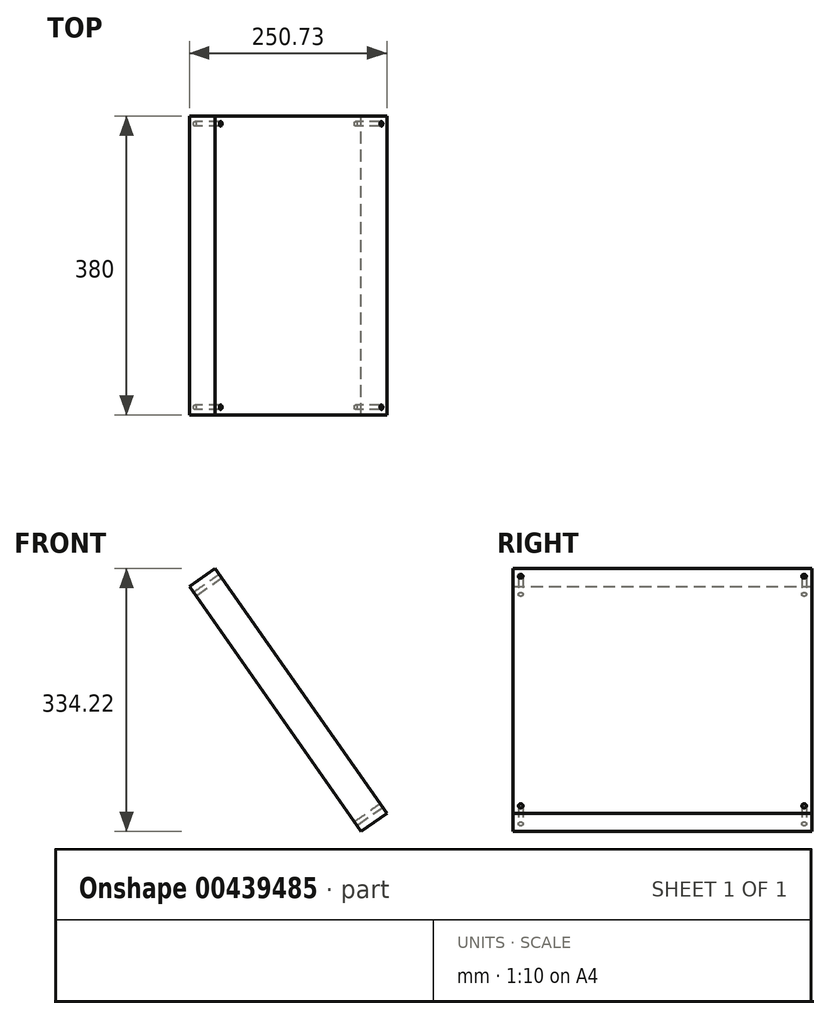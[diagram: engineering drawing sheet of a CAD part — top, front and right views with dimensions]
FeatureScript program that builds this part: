
annotation { "Feature Type Name" : "Feature", "Feature Type Description" : "" }
export const myFeature = defineFeature(function(context is Context, id is Id, definition is map)
    precondition{}
    {
        {
            var Q0;
            Q0=qCreatedBy(makeId("Front.planeOp"),FACE);
            var sketch = newSketch(context, id + "F0", { "sketchPlane" : qUnion([Q0])});
            skLineSegment(sketch, "E0.bottom", {"start": v(-138.5, 149.95) * mm, "end": v(79.46, -161.32) * mm});
            skLineSegment(sketch, "E0.top", {"start": v(-171.27, 127.01) * mm, "end": v(46.69, -184.27) * mm});
            skLineSegment(sketch, "E0.left", {"start": v(-138.5, 149.95) * mm, "end": v(-171.27, 127.01) * mm});
            skLineSegment(sketch, "E0.right", {"start": v(79.46, -161.32) * mm, "end": v(46.69, -184.27) * mm});
            skSolve(sketch);
        }
        {
            var Q0;
            Q0=makeQuery(id+"F0.imprint","IMPRINT",FACE,{"disambiguationData":[TD([[makeQuery(id+"F0.imprint","IMPRINT",EDGE,{"derivedFrom":sQuery(id+"F0.wireOp",EDGE,"E0.bottom")}),-1.0]])]});
            extrude(context, id + "F1", {"entities" : qUnion([Q0]), "depth" : 380 * mm});
        }
        {
            var Q0;
            Q0=makeQuery(id+"F1.opExtrude","SWEPT_FACE",FACE,{"disambiguationData":[OSD([sQuery(id+"F0.wireOp",EDGE,"E0.top")])]});
            var sketch = newSketch(context, id + "F2", { "sketchPlane" : qUnion([Q0])});
            skCircle(sketch, "E1", {"center": v(370, 190.28) * mm, "radius": 3 * mm});
            skLineSegment(sketch, "E2.0", {"start": v(380, 202.28) * mm, "end": v(0, 202.28) * mm});
            skLineSegment(sketch, "E3.0.0", {"start": v(0, 202.28) * mm, "end": v(0, -177.72) * mm});
            skLineSegment(sketch, "E3.0.1", {"start": v(0, -177.72) * mm, "end": v(380, -177.72) * mm});
            skLineSegment(sketch, "E4", {"start": v(190, 202.28) * mm, "end": v(190, -177.72) * mm, "construction": true});
            skLineSegment(sketch, "E5", {"start": v(380, 12.28) * mm, "end": v(190, 12.28) * mm, "construction": true});
            skCircle(sketch, "E6.MirrorC", {"center": v(370, -165.72) * mm, "radius": 3 * mm});
            skCircle(sketch, "E7.MirrorC", {"center": v(10, -165.72) * mm, "radius": 3 * mm});
            skCircle(sketch, "E8.MirrorC", {"center": v(10, 190.28) * mm, "radius": 3 * mm});
            skSolve(sketch);
        }
        {
            var Q0;
            Q0 = qSketchRegion(id + "F2", true);
            extrude(context, id + "F3", {"entities" : qUnion([Q0]), "operationType" : NewBodyOperationType.REMOVE, "endBound" : BoundingType.UP_TO_NEXT, "oppositeDirection" : true, "depth" : 25 * mm});
        }
    });
